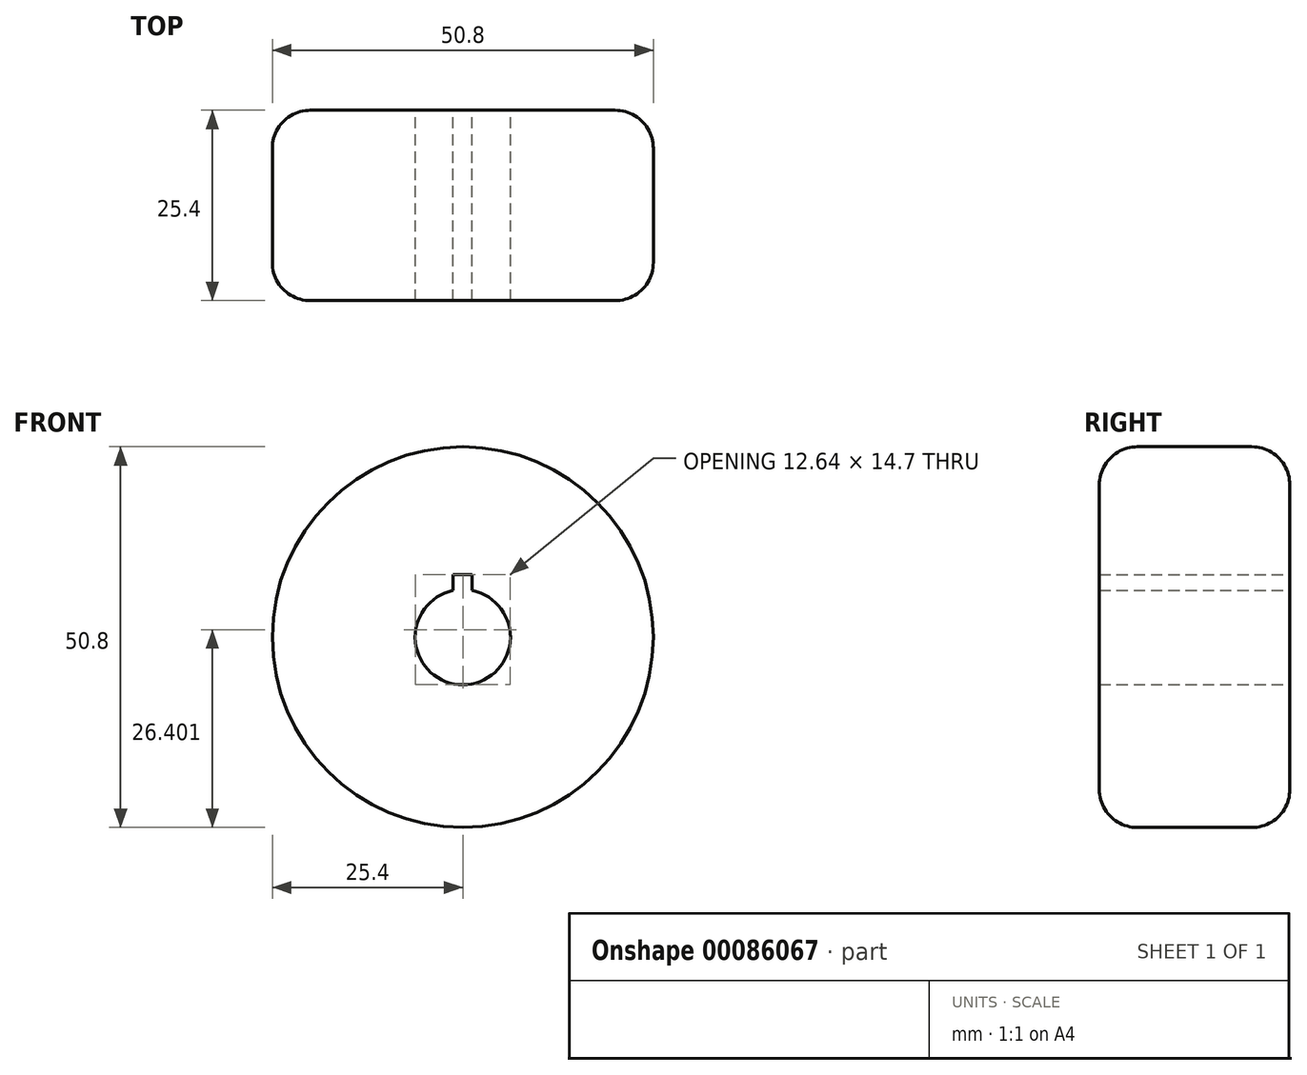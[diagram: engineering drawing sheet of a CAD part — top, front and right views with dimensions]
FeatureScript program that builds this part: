
annotation { "Feature Type Name" : "Feature", "Feature Type Description" : "" }
export const myFeature = defineFeature(function(context is Context, id is Id, definition is map)
    precondition{}
    {
        {
            var Q0;
            Q0=qCreatedBy(makeId("Front.planeOp"),FACE);
            var sketch = newSketch(context, id + "F0", { "sketchPlane" : qUnion([Q0])});
            skCircle(sketch, "E0", {"center": v(0, 0) * mm, "radius": 25.4 * mm});
            skArc(sketch, "E1", {"start": v(-1.27, 6.22) * mm, "mid": v(0, -6.35) * mm, "end": v(1.27, 6.22) * mm});
            skLineSegment(sketch, "E2.bottom", {"start": v(-1.27, 8.35) * mm, "end": v(1.27, 8.35) * mm});
            skLineSegment(sketch, "E2.left", {"start": v(-1.27, 8.35) * mm, "end": v(-1.27, 6.22) * mm});
            skLineSegment(sketch, "E2.right", {"start": v(1.27, 8.35) * mm, "end": v(1.27, 6.22) * mm});
            skPoint(sketch, "E2.top.end.orphan", {"position": v(1.27, -8.35) * mm});
            skPoint(sketch, "E3.trimOffspring.end.orphan", {"position": v(-1.27, -8.35) * mm});
            skSolve(sketch);
        }
        {
            var Q0;
            Q0=makeQuery(id+"F0.imprint","IMPRINT",FACE,{"disambiguationData":[TD([[makeQuery(id+"F0.imprint","IMPRINT",EDGE,{"derivedFrom":sQuery(id+"F0.wireOp",EDGE,"E0")}),1.0]])]});
            extrude(context, id + "F1", {"entities" : qUnion([Q0]), "depth" : 25.4 * mm});
        }
        {
            var Q0;
            Q0=makeQuery(id+"F1.opExtrude","CAP_EDGE",EDGE,{"disambiguationData":[OSD([sQuery(id+"F0.wireOp",EDGE,"E0")])],"isStart":true});
            var Q1;
            Q1=makeQuery(id+"F1.opExtrude","CAP_EDGE",EDGE,{"disambiguationData":[OSD([sQuery(id+"F0.wireOp",EDGE,"E0")])],"isStart":false});
            fillet(context, id + "F2", {"entities" : qUnion([Q0, Q1]), "radius" : 5.08 * mm, "tangentPropagation" : true, "allowEdgeOverflow" : false});
        }
    });
